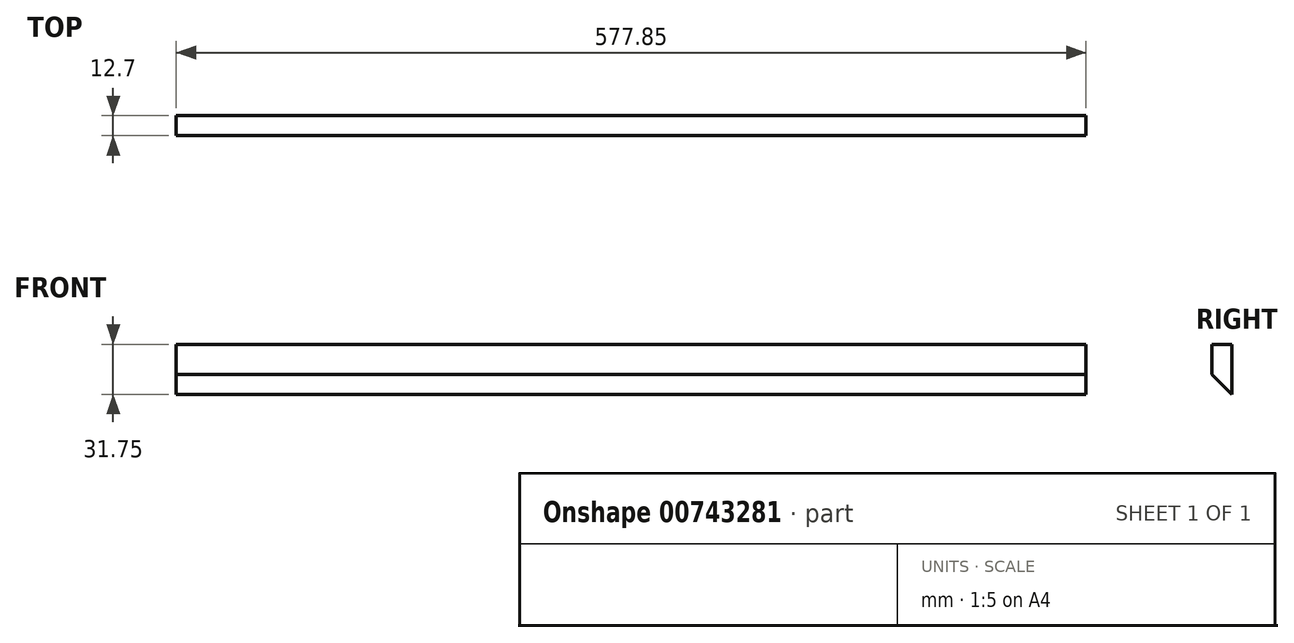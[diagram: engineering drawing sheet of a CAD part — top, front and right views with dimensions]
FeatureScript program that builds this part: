
annotation { "Feature Type Name" : "Feature", "Feature Type Description" : "" }
export const myFeature = defineFeature(function(context is Context, id is Id, definition is map)
    precondition{}
    {
        {
            var Q0;
            Q0=qCreatedBy(makeId("Right.planeOp"),FACE);
            var sketch = newSketch(context, id + "F0", { "sketchPlane" : qUnion([Q0])});
            skLineSegment(sketch, "E0", {"start": v(-6.88, 12.1) * mm, "end": v(5.82, 12.1) * mm});
            skLineSegment(sketch, "E1", {"start": v(5.82, 12.1) * mm, "end": v(5.82, -19.65) * mm});
            skLineSegment(sketch, "E2", {"start": v(5.82, -19.65) * mm, "end": v(-6.88, -6.95) * mm});
            skLineSegment(sketch, "E3", {"start": v(-6.88, -6.95) * mm, "end": v(-6.88, 12.1) * mm});
            skSolve(sketch);
        }
        {
            var Q0;
            Q0=makeQuery(id+"F0.imprint","IMPRINT",FACE,{"disambiguationData":[TD([[makeQuery(id+"F0.imprint","IMPRINT",EDGE,{"derivedFrom":sQuery(id+"F0.wireOp",EDGE,"E0")}),-1.0]])]});
            extrude(context, id + "F1", {"entities" : qUnion([Q0]), "depth" : 577.85 * mm, "offsetDistance" : 25.4 * mm});
        }
    });
